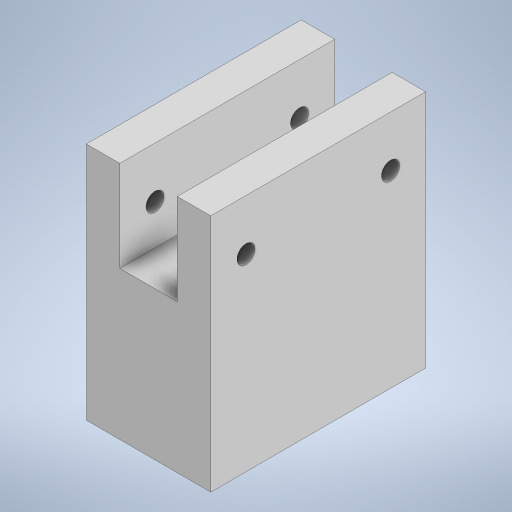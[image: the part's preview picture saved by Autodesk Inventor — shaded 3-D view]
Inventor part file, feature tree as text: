
AUTODESK INVENTOR PART (.ipt)
format: ipt  version: 2024.3 (Build 283343000, 343)  size: 211,968 bytes
history: native  units: mm
features: extrude x3, sketch x3, projected_geometry x1
ambient origin geometry x8: Origin, YZ Plane, XZ Plane, XY Plane, X Axis, Y Axis, Z Axis, Center Point
bodies: Solid1 (feature_tree)
feature tree (7):
  extrude  "Extrusion1"  Depth=44.9mm
  extrude  "Extrusion2"  Depth=50.0mm
  extrude  "Extrusion3"  Depth=12.0mm
  sketch  "Sketch1"  dims[d0=26.0mm d1=44.9mm]
  sketch  "Sketch2"  dims[d2=50.0mm d3=0.0mm d4=6.0mm]
  projected_geometry  "Projected Loop1"
  sketch  "Sketch3"  dims[d5=19.0mm d6=12.0mm d7=50.0mm d8=0.0mm d9=3.8mm d13=50.0mm d14=0.0mm]
